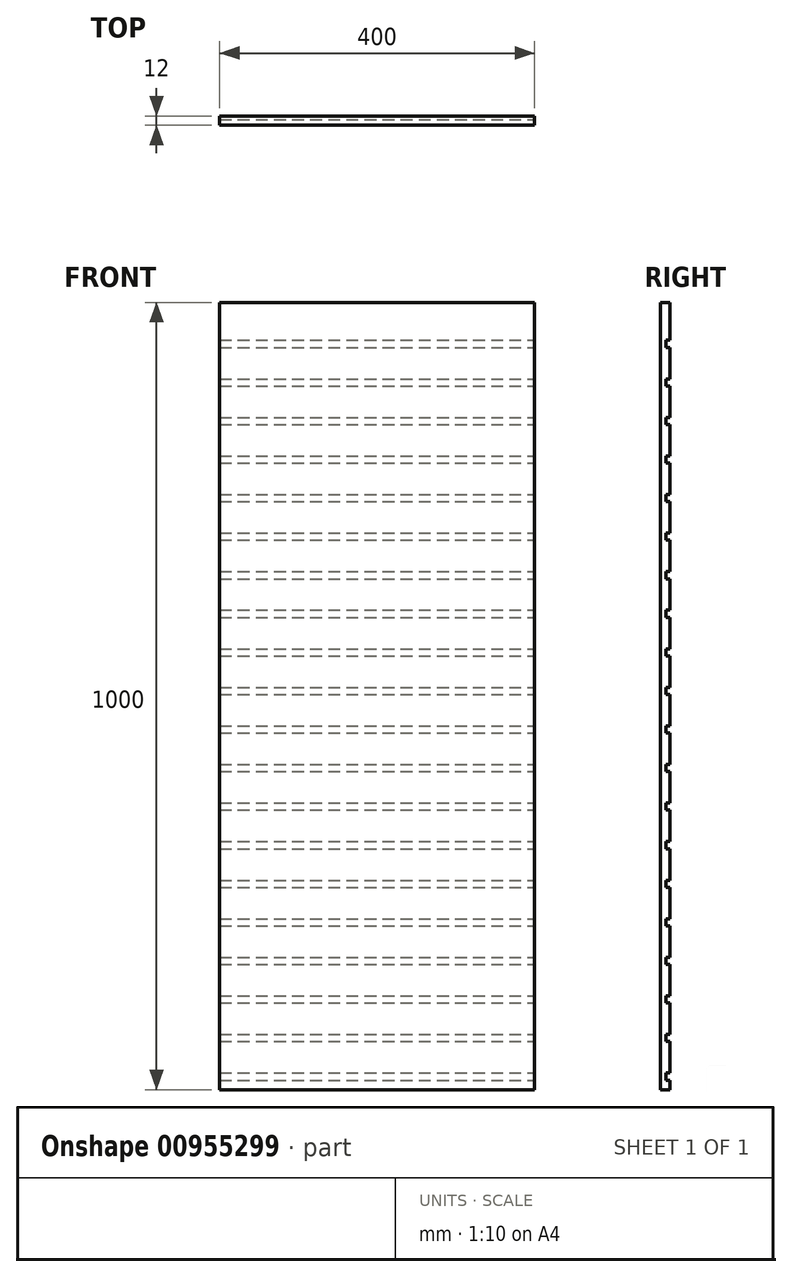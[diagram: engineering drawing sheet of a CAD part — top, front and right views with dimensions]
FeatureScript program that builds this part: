
annotation { "Feature Type Name" : "Feature", "Feature Type Description" : "" }
export const myFeature = defineFeature(function(context is Context, id is Id, definition is map)
    precondition{}
    {
        {
            var Q0;
            Q0=qCreatedBy(makeId("Front.planeOp"),FACE);
            var sketch = newSketch(context, id + "F0", { "sketchPlane" : qUnion([Q0])});
            skLineSegment(sketch, "E0.bottom", {"start": v(-200, 500) * mm, "end": v(200, 500) * mm});
            skLineSegment(sketch, "E0.top", {"start": v(-200, -500) * mm, "end": v(200, -500) * mm});
            skLineSegment(sketch, "E0.left", {"start": v(-200, 500) * mm, "end": v(-200, -500) * mm});
            skLineSegment(sketch, "E0.right", {"start": v(200, 500) * mm, "end": v(200, -500) * mm});
            skPoint(sketch, "E0.middle", {"position": v(0, 0) * mm});
            skSolve(sketch);
        }
        {
            var Q0;
            Q0=makeQuery(id+"F0.imprint","IMPRINT",FACE,{"disambiguationData":[TD([[makeQuery(id+"F0.imprint","IMPRINT",EDGE,{"derivedFrom":sQuery(id+"F0.wireOp",EDGE,"E0.bottom")}),-1.0]])]});
            var sketch = newSketch(context, id + "F1", { "sketchPlane" : qUnion([Q0])});
            skLineSegment(sketch, "E1.bottom", {"start": v(-200, -488) * mm, "end": v(200, -488) * mm});
            skLineSegment(sketch, "E1.top", {"start": v(-200, -479) * mm, "end": v(200, -479) * mm});
            skLineSegment(sketch, "E1.left", {"start": v(-200, -488) * mm, "end": v(-200, -479) * mm});
            skLineSegment(sketch, "E1.right", {"start": v(200, -488) * mm, "end": v(200, -479) * mm});
            skPoint(sketch, "E1.middle", {"position": v(0, -483.5) * mm});
            skPoint(sketch, "E2.0.1.0", {"position": v(0, -434.5) * mm});
            skLineSegment(sketch, "E2.0.1.1", {"start": v(-200, -439) * mm, "end": v(200, -439) * mm});
            skLineSegment(sketch, "E2.0.1.2", {"start": v(-200, -430) * mm, "end": v(200, -430) * mm});
            skLineSegment(sketch, "E2.0.1.3", {"start": v(200, -439) * mm, "end": v(200, -430) * mm});
            skLineSegment(sketch, "E2.0.1.4", {"start": v(-200, -439) * mm, "end": v(-200, -430) * mm});
            skPoint(sketch, "E2.0.2.0", {"position": v(0, -385.5) * mm});
            skLineSegment(sketch, "E2.0.2.1", {"start": v(-200, -390) * mm, "end": v(200, -390) * mm});
            skLineSegment(sketch, "E2.0.2.2", {"start": v(-200, -381) * mm, "end": v(200, -381) * mm});
            skLineSegment(sketch, "E2.0.2.3", {"start": v(200, -390) * mm, "end": v(200, -381) * mm});
            skLineSegment(sketch, "E2.0.2.4", {"start": v(-200, -390) * mm, "end": v(-200, -381) * mm});
            skPoint(sketch, "E2.0.3.0", {"position": v(0, -336.5) * mm});
            skLineSegment(sketch, "E2.0.3.1", {"start": v(-200, -341) * mm, "end": v(200, -341) * mm});
            skLineSegment(sketch, "E2.0.3.2", {"start": v(-200, -332) * mm, "end": v(200, -332) * mm});
            skLineSegment(sketch, "E2.0.3.3", {"start": v(200, -341) * mm, "end": v(200, -332) * mm});
            skLineSegment(sketch, "E2.0.3.4", {"start": v(-200, -341) * mm, "end": v(-200, -332) * mm});
            skPoint(sketch, "E2.0.4.0", {"position": v(0, -287.5) * mm});
            skLineSegment(sketch, "E2.0.4.1", {"start": v(-200, -292) * mm, "end": v(200, -292) * mm});
            skLineSegment(sketch, "E2.0.4.2", {"start": v(-200, -283) * mm, "end": v(200, -283) * mm});
            skLineSegment(sketch, "E2.0.4.3", {"start": v(200, -292) * mm, "end": v(200, -283) * mm});
            skLineSegment(sketch, "E2.0.4.4", {"start": v(-200, -292) * mm, "end": v(-200, -283) * mm});
            skPoint(sketch, "E2.0.5.0", {"position": v(0, -238.5) * mm});
            skLineSegment(sketch, "E2.0.5.1", {"start": v(-200, -243) * mm, "end": v(200, -243) * mm});
            skLineSegment(sketch, "E2.0.5.2", {"start": v(-200, -234) * mm, "end": v(200, -234) * mm});
            skLineSegment(sketch, "E2.0.5.3", {"start": v(200, -243) * mm, "end": v(200, -234) * mm});
            skLineSegment(sketch, "E2.0.5.4", {"start": v(-200, -243) * mm, "end": v(-200, -234) * mm});
            skPoint(sketch, "E2.0.6.0", {"position": v(0, -189.5) * mm});
            skLineSegment(sketch, "E2.0.6.1", {"start": v(-200, -194) * mm, "end": v(200, -194) * mm});
            skLineSegment(sketch, "E2.0.6.2", {"start": v(-200, -185) * mm, "end": v(200, -185) * mm});
            skLineSegment(sketch, "E2.0.6.3", {"start": v(200, -194) * mm, "end": v(200, -185) * mm});
            skLineSegment(sketch, "E2.0.6.4", {"start": v(-200, -194) * mm, "end": v(-200, -185) * mm});
            skPoint(sketch, "E2.0.7.0", {"position": v(0, -140.5) * mm});
            skLineSegment(sketch, "E2.0.7.1", {"start": v(-200, -145) * mm, "end": v(200, -145) * mm});
            skLineSegment(sketch, "E2.0.7.2", {"start": v(-200, -136) * mm, "end": v(200, -136) * mm});
            skLineSegment(sketch, "E2.0.7.3", {"start": v(200, -145) * mm, "end": v(200, -136) * mm});
            skLineSegment(sketch, "E2.0.7.4", {"start": v(-200, -145) * mm, "end": v(-200, -136) * mm});
            skPoint(sketch, "E2.0.8.0", {"position": v(0, -91.5) * mm});
            skLineSegment(sketch, "E2.0.8.1", {"start": v(-200, -96) * mm, "end": v(200, -96) * mm});
            skLineSegment(sketch, "E2.0.8.2", {"start": v(-200, -87) * mm, "end": v(200, -87) * mm});
            skLineSegment(sketch, "E2.0.8.3", {"start": v(200, -96) * mm, "end": v(200, -87) * mm});
            skLineSegment(sketch, "E2.0.8.4", {"start": v(-200, -96) * mm, "end": v(-200, -87) * mm});
            skPoint(sketch, "E2.0.9.0", {"position": v(0, -42.5) * mm});
            skLineSegment(sketch, "E2.0.9.1", {"start": v(-200, -47) * mm, "end": v(200, -47) * mm});
            skLineSegment(sketch, "E2.0.9.2", {"start": v(-200, -38) * mm, "end": v(200, -38) * mm});
            skLineSegment(sketch, "E2.0.9.3", {"start": v(200, -47) * mm, "end": v(200, -38) * mm});
            skLineSegment(sketch, "E2.0.9.4", {"start": v(-200, -47) * mm, "end": v(-200, -38) * mm});
            skPoint(sketch, "E2.0.10.0", {"position": v(0, 6.5) * mm});
            skLineSegment(sketch, "E2.0.10.1", {"start": v(-200, 2) * mm, "end": v(200, 2) * mm});
            skLineSegment(sketch, "E2.0.10.2", {"start": v(-200, 11) * mm, "end": v(200, 11) * mm});
            skLineSegment(sketch, "E2.0.10.3", {"start": v(200, 2) * mm, "end": v(200, 11) * mm});
            skLineSegment(sketch, "E2.0.10.4", {"start": v(-200, 2) * mm, "end": v(-200, 11) * mm});
            skPoint(sketch, "E2.0.11.0", {"position": v(0, 55.5) * mm});
            skLineSegment(sketch, "E2.0.11.1", {"start": v(-200, 51) * mm, "end": v(200, 51) * mm});
            skLineSegment(sketch, "E2.0.11.2", {"start": v(-200, 60) * mm, "end": v(200, 60) * mm});
            skLineSegment(sketch, "E2.0.11.3", {"start": v(200, 51) * mm, "end": v(200, 60) * mm});
            skLineSegment(sketch, "E2.0.11.4", {"start": v(-200, 51) * mm, "end": v(-200, 60) * mm});
            skPoint(sketch, "E2.0.12.0", {"position": v(0, 104.5) * mm});
            skLineSegment(sketch, "E2.0.12.1", {"start": v(-200, 100) * mm, "end": v(200, 100) * mm});
            skLineSegment(sketch, "E2.0.12.2", {"start": v(-200, 109) * mm, "end": v(200, 109) * mm});
            skLineSegment(sketch, "E2.0.12.3", {"start": v(200, 100) * mm, "end": v(200, 109) * mm});
            skLineSegment(sketch, "E2.0.12.4", {"start": v(-200, 100) * mm, "end": v(-200, 109) * mm});
            skPoint(sketch, "E2.0.13.0", {"position": v(0, 153.5) * mm});
            skLineSegment(sketch, "E2.0.13.1", {"start": v(-200, 149) * mm, "end": v(200, 149) * mm});
            skLineSegment(sketch, "E2.0.13.2", {"start": v(-200, 158) * mm, "end": v(200, 158) * mm});
            skLineSegment(sketch, "E2.0.13.3", {"start": v(200, 149) * mm, "end": v(200, 158) * mm});
            skLineSegment(sketch, "E2.0.13.4", {"start": v(-200, 149) * mm, "end": v(-200, 158) * mm});
            skPoint(sketch, "E2.0.14.0", {"position": v(0, 202.5) * mm});
            skLineSegment(sketch, "E2.0.14.1", {"start": v(-200, 198) * mm, "end": v(200, 198) * mm});
            skLineSegment(sketch, "E2.0.14.2", {"start": v(-200, 207) * mm, "end": v(200, 207) * mm});
            skLineSegment(sketch, "E2.0.14.3", {"start": v(200, 198) * mm, "end": v(200, 207) * mm});
            skLineSegment(sketch, "E2.0.14.4", {"start": v(-200, 198) * mm, "end": v(-200, 207) * mm});
            skPoint(sketch, "E2.0.15.0", {"position": v(0, 251.5) * mm});
            skLineSegment(sketch, "E2.0.15.1", {"start": v(-200, 247) * mm, "end": v(200, 247) * mm});
            skLineSegment(sketch, "E2.0.15.2", {"start": v(-200, 256) * mm, "end": v(200, 256) * mm});
            skLineSegment(sketch, "E2.0.15.3", {"start": v(200, 247) * mm, "end": v(200, 256) * mm});
            skLineSegment(sketch, "E2.0.15.4", {"start": v(-200, 247) * mm, "end": v(-200, 256) * mm});
            skPoint(sketch, "E2.0.16.0", {"position": v(0, 300.5) * mm});
            skLineSegment(sketch, "E2.0.16.1", {"start": v(-200, 296) * mm, "end": v(200, 296) * mm});
            skLineSegment(sketch, "E2.0.16.2", {"start": v(-200, 305) * mm, "end": v(200, 305) * mm});
            skLineSegment(sketch, "E2.0.16.3", {"start": v(200, 296) * mm, "end": v(200, 305) * mm});
            skLineSegment(sketch, "E2.0.16.4", {"start": v(-200, 296) * mm, "end": v(-200, 305) * mm});
            skPoint(sketch, "E2.0.17.0", {"position": v(0, 349.5) * mm});
            skLineSegment(sketch, "E2.0.17.1", {"start": v(-200, 345) * mm, "end": v(200, 345) * mm});
            skLineSegment(sketch, "E2.0.17.2", {"start": v(-200, 354) * mm, "end": v(200, 354) * mm});
            skLineSegment(sketch, "E2.0.17.3", {"start": v(200, 345) * mm, "end": v(200, 354) * mm});
            skLineSegment(sketch, "E2.0.17.4", {"start": v(-200, 345) * mm, "end": v(-200, 354) * mm});
            skPoint(sketch, "E2.0.18.0", {"position": v(0, 398.5) * mm});
            skLineSegment(sketch, "E2.0.18.1", {"start": v(-200, 394) * mm, "end": v(200, 394) * mm});
            skLineSegment(sketch, "E2.0.18.2", {"start": v(-200, 403) * mm, "end": v(200, 403) * mm});
            skLineSegment(sketch, "E2.0.18.3", {"start": v(200, 394) * mm, "end": v(200, 403) * mm});
            skLineSegment(sketch, "E2.0.18.4", {"start": v(-200, 394) * mm, "end": v(-200, 403) * mm});
            skPoint(sketch, "E2.0.19.0", {"position": v(0, 447.5) * mm});
            skLineSegment(sketch, "E2.0.19.1", {"start": v(-200, 443) * mm, "end": v(200, 443) * mm});
            skLineSegment(sketch, "E2.0.19.2", {"start": v(-200, 452) * mm, "end": v(200, 452) * mm});
            skLineSegment(sketch, "E2.0.19.3", {"start": v(200, 443) * mm, "end": v(200, 452) * mm});
            skLineSegment(sketch, "E2.0.19.4", {"start": v(-200, 443) * mm, "end": v(-200, 452) * mm});
            skLineSegment(sketch, "E2.direction1", {"start": v(-200, -488) * mm, "end": v(-175, -488) * mm, "construction": true});
            skLineSegment(sketch, "E2.direction2", {"start": v(-200, -488) * mm, "end": v(-200, -439) * mm, "construction": true});
            skSolve(sketch);
        }
        {
            var Q0;
            Q0 = qSketchRegion(id + "F0", true);
            extrude(context, id + "F2", {"entities" : qUnion([Q0]), "depth" : 12 * mm, "offsetDistance" : 25 * mm});
        }
        {
            var Q0;
            Q0 = qSketchRegion(id + "F1", true);
            extrude(context, id + "F3", {"entities" : qUnion([Q0]), "operationType" : NewBodyOperationType.REMOVE, "depth" : 5 * mm, "offsetDistance" : 25 * mm});
        }
    });
